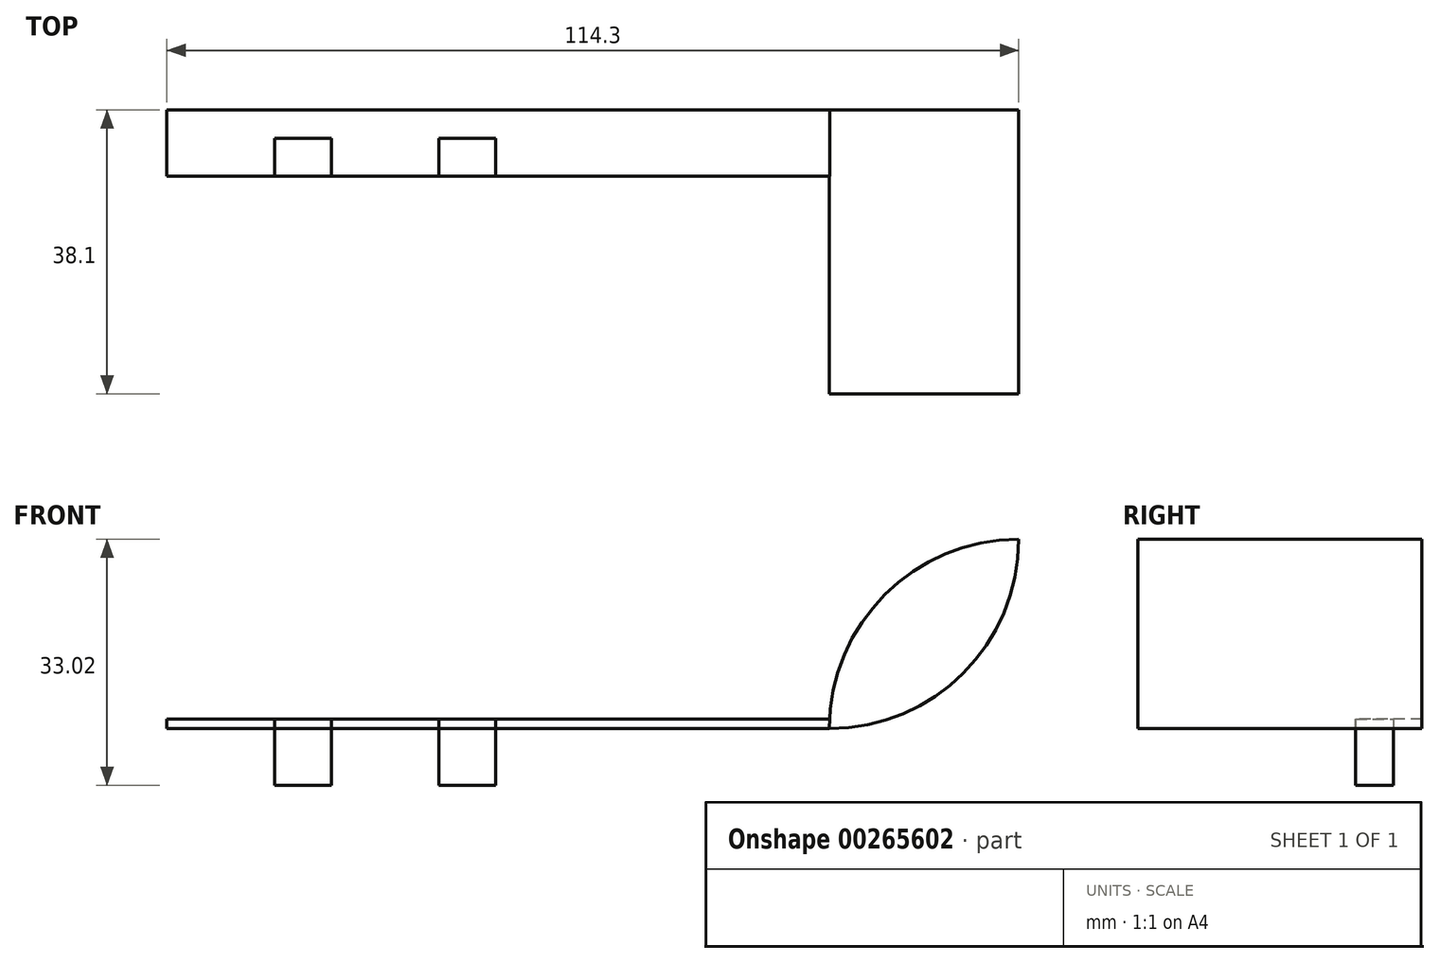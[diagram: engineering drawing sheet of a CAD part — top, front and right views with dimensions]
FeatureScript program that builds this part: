
annotation { "Feature Type Name" : "Feature", "Feature Type Description" : "" }
export const myFeature = defineFeature(function(context is Context, id is Id, definition is map)
    precondition{}
    {
        {
            var Q0;
            Q0=qCreatedBy(makeId("Top.planeOp"),FACE);
            var sketch = newSketch(context, id + "F0", { "sketchPlane" : qUnion([Q0])});
            skLineSegment(sketch, "E0.bottom", {"start": v(-145.43, 32.32) * mm, "end": v(-56.53, 32.32) * mm});
            skLineSegment(sketch, "E0.top", {"start": v(-145.43, 23.43) * mm, "end": v(-56.53, 23.43) * mm});
            skLineSegment(sketch, "E0.left", {"start": v(-145.43, 32.32) * mm, "end": v(-145.43, 23.43) * mm});
            skLineSegment(sketch, "E0.right", {"start": v(-56.53, 32.32) * mm, "end": v(-56.53, 23.43) * mm});
            skLineSegment(sketch, "E1", {"start": v(-86.78, 37.64) * mm, "end": v(-86.78, 0) * mm, "construction": true});
            skLineSegment(sketch, "E2", {"start": v(-130.98, 23.43) * mm, "end": v(-130.98, 28.5) * mm});
            skLineSegment(sketch, "E3", {"start": v(-130.98, 28.5) * mm, "end": v(-123.36, 28.5) * mm});
            skLineSegment(sketch, "E4", {"start": v(-123.36, 28.5) * mm, "end": v(-123.36, 23.43) * mm});
            skLineSegment(sketch, "E5", {"start": v(-108.9, 23.43) * mm, "end": v(-108.9, 28.5) * mm});
            skLineSegment(sketch, "E6", {"start": v(-108.9, 28.5) * mm, "end": v(-101.29, 28.5) * mm});
            skLineSegment(sketch, "E7", {"start": v(-101.29, 28.5) * mm, "end": v(-101.29, 23.43) * mm});
            skLineSegment(sketch, "E8", {"start": v(-56.53, 32.32) * mm, "end": v(-31.13, 32.32) * mm});
            skLineSegment(sketch, "E9", {"start": v(-31.13, 32.32) * mm, "end": v(-31.13, -5.78) * mm});
            skLineSegment(sketch, "E10", {"start": v(-31.13, -5.78) * mm, "end": v(-56.53, -5.78) * mm});
            skLineSegment(sketch, "E11", {"start": v(-56.53, -5.78) * mm, "end": v(-56.53, 23.43) * mm});
            skSolve(sketch);
        }
        {
            var Q0;
            Q0=makeQuery(id+"F0.imprint","IMPRINT",FACE,{"disambiguationData":[TD([[makeQuery(id+"F0.imprint","IMPRINT",EDGE,{"derivedFrom":sQuery(id+"F0.wireOp",EDGE,"E0.bottom")}),-1.0]])]});
            extrude(context, id + "F1", {"entities" : qUnion([Q0]), "depth" : 1.27 * mm});
        }
        {
            var Q0;
            {var subQ0=sQuery(id+"F0.wireOp",EDGE,"E2");Q0=makeQuery(id+"F0.imprint","IMPRINT",FACE,{"disambiguationData":[TD([[makeQuery(id+"F0.imprint","IMPRINT",EDGE,{"derivedFrom":subQ0}),-1.0]])]});}
            var Q1;
            {var subQ0=sQuery(id+"F0.wireOp",EDGE,"E5");Q1=makeQuery(id+"F0.imprint","IMPRINT",FACE,{"disambiguationData":[TD([[makeQuery(id+"F0.imprint","IMPRINT",EDGE,{"derivedFrom":subQ0}),-1.0]])]});}
            extrude(context, id + "F2", {"entities" : qUnion([Q0, Q1]), "oppositeDirection" : true, "depth" : 7.62 * mm});
        }
        {
            var Q0;
            {var subQ0=sQuery(id+"F0.wireOp",EDGE,"E2");Q0=makeQuery(id+"F0.imprint","IMPRINT",FACE,{"disambiguationData":[TD([[makeQuery(id+"F0.imprint","IMPRINT",EDGE,{"derivedFrom":subQ0}),-1.0]])]});}
            var Q1;
            {var subQ0=sQuery(id+"F0.wireOp",EDGE,"E5");Q1=makeQuery(id+"F0.imprint","IMPRINT",FACE,{"disambiguationData":[TD([[makeQuery(id+"F0.imprint","IMPRINT",EDGE,{"derivedFrom":subQ0}),-1.0]])]});}
            extrude(context, id + "F3", {"entities" : qUnion([Q0, Q1]), "depth" : 1.27 * mm});
        }
        {
            var Q0;
            Q0=makeQuery(id+"F0.imprint","IMPRINT",FACE,{"disambiguationData":[TD([[makeQuery(id+"F0.imprint","IMPRINT",EDGE,{"derivedFrom":sQuery(id+"F0.wireOp",EDGE,"E0.right")}),1.0]])]});
            extrude(context, id + "F4", {"entities" : qUnion([Q0]), "operationType" : NewBodyOperationType.ADD, "depth" : 25.4 * mm});
        }
        {
            var Q0;
            Q0=makeQuery(id+"F4.opExtrude","CAP_EDGE",EDGE,{"disambiguationData":[OSD([sQuery(id+"F0.wireOp",EDGE,"E9")])],"isStart":true});
            fillet(context, id + "F5", {"entities" : qUnion([Q0]), "radius" : 25.4 * mm, "tangentPropagation" : true, "allowEdgeOverflow" : false});
        }
        {
            var Q0;
            Q0=makeQuery(id+"F4.opExtrude","CAP_EDGE",EDGE,{"disambiguationData":[OSD([sQuery(id+"F0.wireOp",EDGE,"E0.right"),sQuery(id+"F0.wireOp",EDGE,"E11")])],"isStart":false});
            fillet(context, id + "F6", {"entities" : qUnion([Q0]), "radius" : 25.4 * mm, "tangentPropagation" : true, "allowEdgeOverflow" : false});
        }
    });
